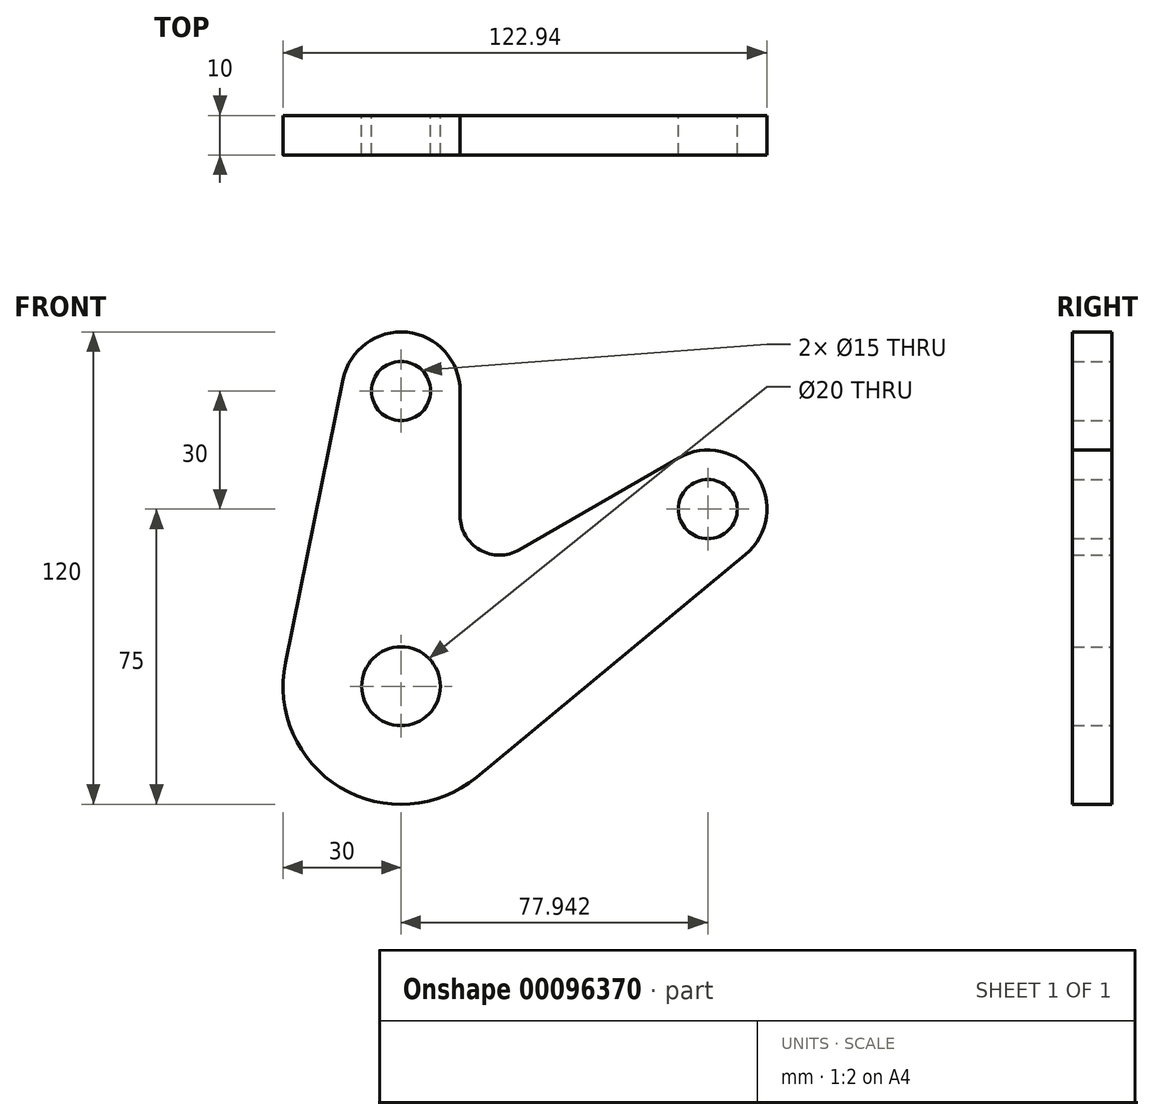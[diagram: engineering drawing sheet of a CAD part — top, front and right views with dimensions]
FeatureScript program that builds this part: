
annotation { "Feature Type Name" : "Feature", "Feature Type Description" : "" }
export const myFeature = defineFeature(function(context is Context, id is Id, definition is map)
    precondition{}
    {
        {
            var Q0;
            Q0=qCreatedBy(makeId("Front.planeOp"),FACE);
            var sketch = newSketch(context, id + "F0", { "sketchPlane" : qUnion([Q0])});
            skLineSegment(sketch, "E0", {"start": v(15, 75) * mm, "end": v(15, 43.3) * mm});
            skArc(sketch, "E1", {"start": v(70.44, 58) * mm, "mid": v(90.26, 53.56) * mm, "end": v(87.5, 33.44) * mm});
            skLineSegment(sketch, "E2", {"start": v(19.12, -23.12) * mm, "end": v(87.5, 33.44) * mm});
            skCircle(sketch, "E3", {"center": v(0, 75) * mm, "radius": 7.5 * mm});
            skCircle(sketch, "E4", {"center": v(77.94, 45) * mm, "radius": 7.5 * mm});
            skCircle(sketch, "E5", {"center": v(0, 0) * mm, "radius": 10 * mm});
            skLineSegment(sketch, "E6", {"start": v(70.44, 58) * mm, "end": v(30, 34.64) * mm});
            skLineSegment(sketch, "E7", {"start": v(-29.4, 6) * mm, "end": v(-14.7, 78) * mm});
            skArc(sketch, "E8", {"start": v(19.12, -23.12) * mm, "mid": v(-15.44, -25.72) * mm, "end": v(-29.4, 6) * mm});
            skArc(sketch, "E9", {"start": v(15, 75) * mm, "mid": v(1.5, 89.92) * mm, "end": v(-14.7, 78) * mm});
            skArc(sketch, "E10", {"start": v(15, 43.3) * mm, "mid": v(20, 34.64) * mm, "end": v(30, 34.64) * mm});
            skLineSegment(sketch, "E11", {"start": v(0, 75) * mm, "end": v(0, 0) * mm, "construction": true});
            skLineSegment(sketch, "E12", {"start": v(0, 0) * mm, "end": v(77.94, 45) * mm, "construction": true});
            skSolve(sketch);
        }
        {
            var Q0;
            Q0=makeQuery(id+"F0.imprint","IMPRINT",FACE,{"disambiguationData":[TD([[makeQuery(id+"F0.imprint","IMPRINT",EDGE,{"derivedFrom":sQuery(id+"F0.wireOp",EDGE,"E0")}),-1.0]])]});
            extrude(context, id + "F1", {"entities" : qUnion([Q0]), "depth" : 10 * mm});
        }
    });
